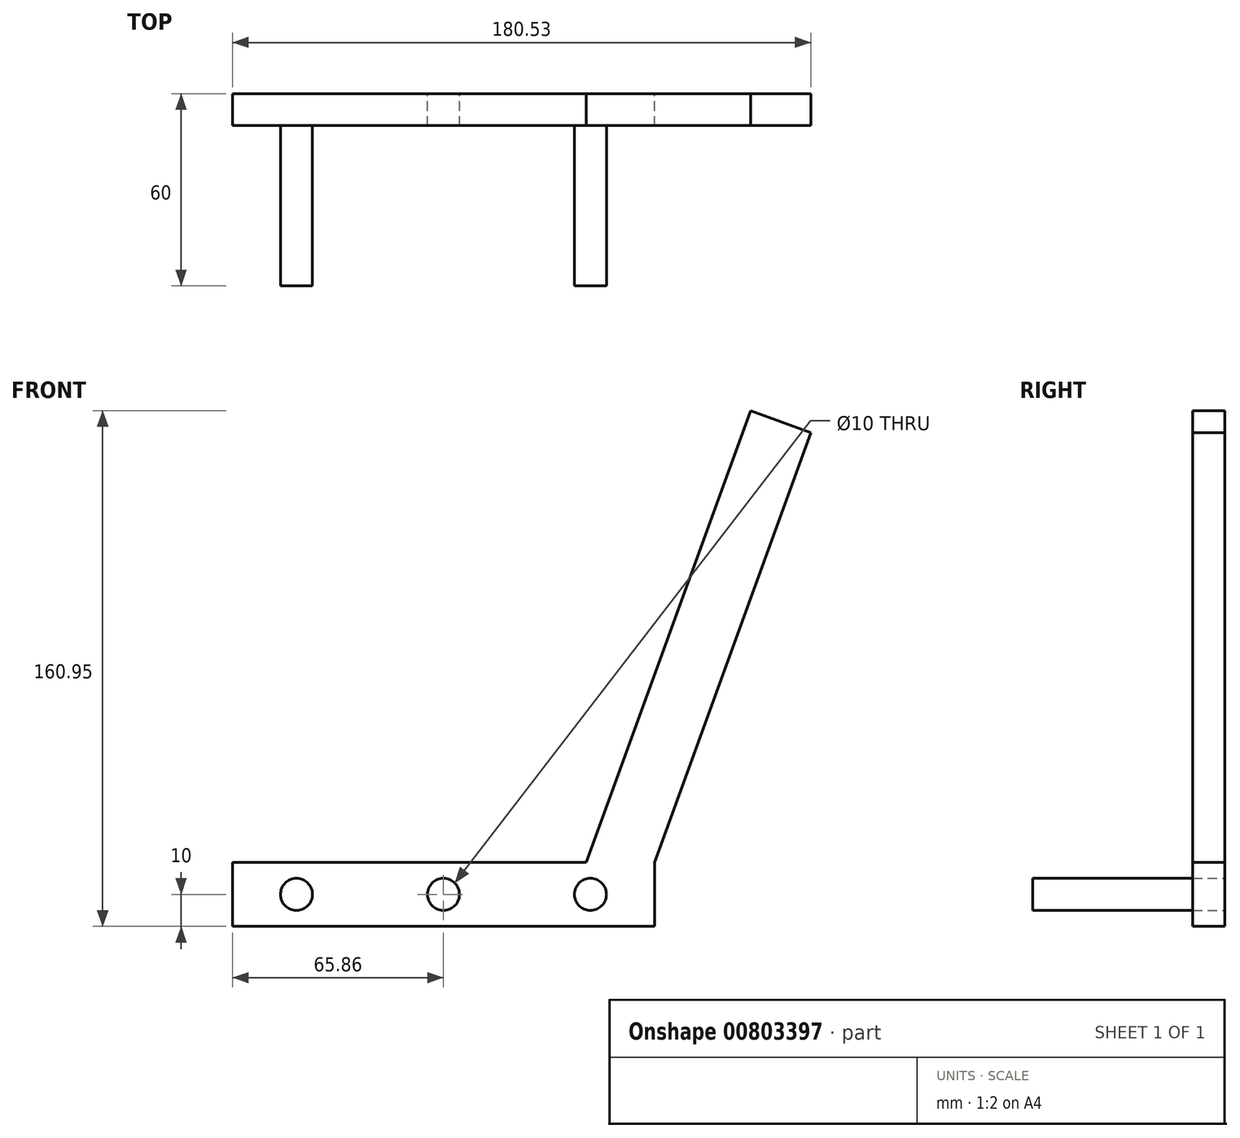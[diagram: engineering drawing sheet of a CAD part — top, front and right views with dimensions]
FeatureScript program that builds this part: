
annotation { "Feature Type Name" : "Feature", "Feature Type Description" : "" }
export const myFeature = defineFeature(function(context is Context, id is Id, definition is map)
    precondition{}
    {
        {
            var Q0;
            Q0=qCreatedBy(makeId("Front.planeOp"),FACE);
            var sketch = newSketch(context, id + "F0", { "sketchPlane" : qUnion([Q0])});
            skLineSegment(sketch, "E0.bottom", {"start": v(-65.86, -10) * mm, "end": v(65.86, -10) * mm});
            skLineSegment(sketch, "E0.top", {"start": v(-65.86, 10) * mm, "end": v(65.86, 10) * mm});
            skLineSegment(sketch, "E0.left", {"start": v(-65.86, -10) * mm, "end": v(-65.86, 10) * mm});
            skLineSegment(sketch, "E0.right", {"start": v(65.86, -10) * mm, "end": v(65.86, 10) * mm});
            skPoint(sketch, "E0.middle", {"position": v(0, 0) * mm});
            skLineSegment(sketch, "E1", {"start": v(-65.86, 0) * mm, "end": v(65.86, 0) * mm, "construction": true});
            skCircle(sketch, "E2", {"center": v(0, 0) * mm, "radius": 5 * mm});
            skSolve(sketch);
        }
        {
            var Q0;
            Q0=makeQuery(id+"F0.imprint","IMPRINT",FACE,{"disambiguationData":[TD([[makeQuery(id+"F0.imprint","IMPRINT",EDGE,{"derivedFrom":sQuery(id+"F0.wireOp",EDGE,"E0.bottom")}),1.0]])]});
            extrude(context, id + "F1", {"entities" : qUnion([Q0]), "depth" : 10 * mm, "offsetDistance" : 25 * mm});
        }
        {
            var Q0;
            Q0=makeQuery(id+"F1.opExtrude","CAP_FACE",FACE,{"disambiguationData":[OSD([sQuery(id+"F0.wireOp",EDGE,"E0.bottom"),sQuery(id+"F0.wireOp",EDGE,"E0.top"),sQuery(id+"F0.wireOp",EDGE,"E0.left"),sQuery(id+"F0.wireOp",EDGE,"E0.right"),sQuery(id+"F0.wireOp",EDGE,"E2")])],"isStart":false});
            var sketch = newSketch(context, id + "F2", { "sketchPlane" : qUnion([Q0])});
            skCircle(sketch, "E3", {"center": v(-45.86, 0) * mm, "radius": 5 * mm});
            skCircle(sketch, "E4", {"center": v(45.86, 0) * mm, "radius": 5 * mm});
            skSolve(sketch);
        }
        {
            var Q0;
            Q0=makeQuery(id+"F2.imprint","IMPRINT",FACE,{"disambiguationData":[TD([[makeQuery(id+"F2.imprint","IMPRINT",EDGE,{"derivedFrom":sQuery(id+"F2.wireOp",EDGE,"E3")}),1.0]])]});
            var Q1;
            Q1=makeQuery(id+"F2.imprint","IMPRINT",FACE,{"disambiguationData":[TD([[makeQuery(id+"F2.imprint","IMPRINT",EDGE,{"derivedFrom":sQuery(id+"F2.wireOp",EDGE,"E4")}),1.0]])]});
            extrude(context, id + "F3", {"entities" : qUnion([Q0, Q1]), "operationType" : NewBodyOperationType.ADD, "depth" : 50 * mm, "offsetDistance" : 25 * mm});
        }
        {
            var Q0;
            Q0=qCreatedBy(makeId("Front.planeOp"),FACE);
            var sketch = newSketch(context, id + "F4", { "sketchPlane" : qUnion([Q0])});
            skLineSegment(sketch, "E5", {"start": v(44.58, 10) * mm, "end": v(95.88, 150.95) * mm});
            skLineSegment(sketch, "E6", {"start": v(95.88, 150.95) * mm, "end": v(114.67, 144.11) * mm});
            skLineSegment(sketch, "E7", {"start": v(114.67, 144.11) * mm, "end": v(63.37, 3.16) * mm});
            skLineSegment(sketch, "E8", {"start": v(63.37, 3.16) * mm, "end": v(44.58, 10) * mm});
            skSolve(sketch);
        }
        {
            var Q0;
            Q0=makeQuery(id+"F4.imprint","IMPRINT",FACE,{"disambiguationData":[TD([[makeQuery(id+"F4.imprint","IMPRINT",EDGE,{"derivedFrom":sQuery(id+"F4.wireOp",EDGE,"E5")}),-1.0]])]});
            extrude(context, id + "F5", {"entities" : qUnion([Q0]), "operationType" : NewBodyOperationType.ADD, "depth" : 10 * mm, "offsetDistance" : 25 * mm});
        }
    });
